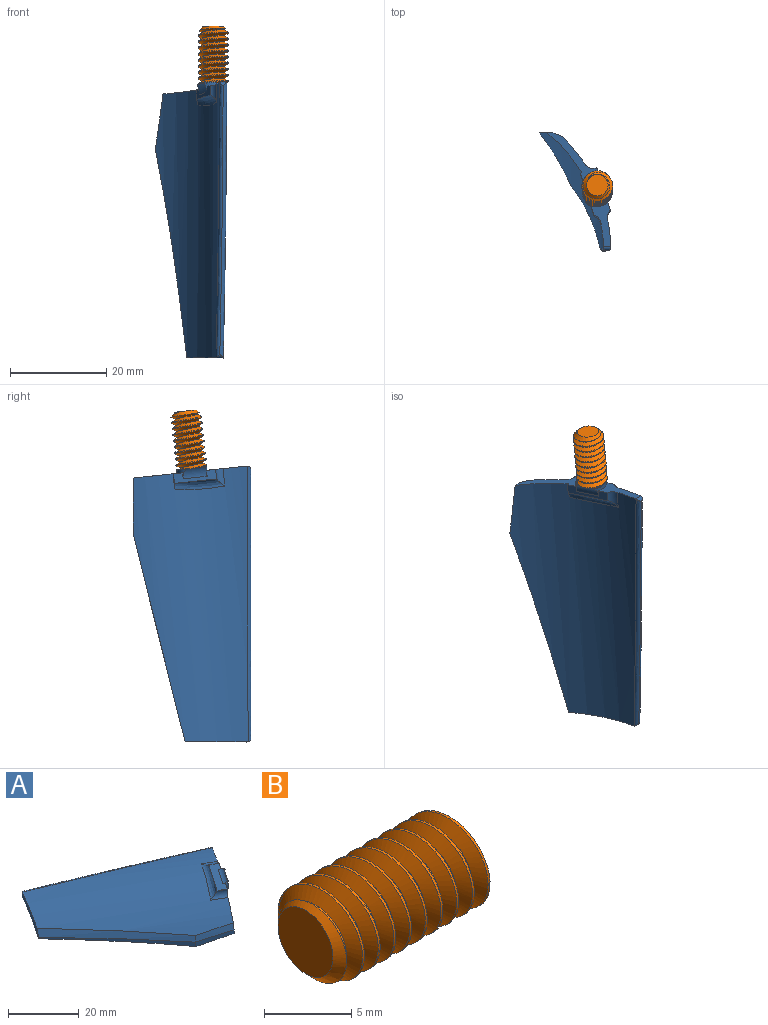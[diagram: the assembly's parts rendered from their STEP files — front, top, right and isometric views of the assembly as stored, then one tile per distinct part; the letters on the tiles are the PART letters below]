
ASSEMBLY  parts=2 mates=1
PART A: 35 faces, bbox 98.5x57.7x16.1 mm
  f0: cylinder r=31.75mm len=61.98mm, axis (0.87,-0.5,0), area 1229.6mm2, adj f8,f10,f11,f12,f13,f14,f15,f16
  f1: cylinder r=33.27mm len=61.61mm, axis (0.87,-0.5,0), area 1109.5mm2, adj f6,f7,f9,f11,f12,f15,f16,f19
  f2: cylinder r=3.17mm len=4.73mm, axis (-0.87,0.5,0), area 3.6mm2, adj f4,f5,f15,f17,f22,f26,f27
  f3: cylinder r=3.17mm len=4.72mm, axis (-0.87,0.5,0), area 3.6mm2, adj f4,f5,f16,f17,f22,f26,f28
  f4: plane 3.52x2.06mm, normal (-0.72,0.16,0.67), area 0.7mm2, adj f2,f3,f22,f27,f28,f29,f30,f31
  f5: plane 8.76x6.27mm, normal (0.15,0.27,-0.95), area 12mm2, adj f2,f3,f15,f16,f23,f24,f25,f26
  f6: bspline ~39.82x31.49mm, area 102.7mm2, adj f1,f7,f12,f13
  f7: bspline ~11.97x5.98mm, area 22.9mm2, adj f1,f6,f14,f16
  f8: cylinder r=0.76mm len=1.54mm, axis (0,0,1), area 1.2mm2, adj f0,f9,f10,f12
  f9: bspline ~98.35x44.27mm, area 73.1mm2, adj f1,f8,f10,f11,f12
  f10: bspline ~52.65x24.02mm, area 63mm2, adj f0,f8,f9,f11
  f11: cylinder r=0.76mm len=1.53mm, axis (0,0,-1), area 1.3mm2, adj f0,f1,f9,f10,f15
  f12: plane 11.9x7.69mm, normal (-0.91,0.41,0), area 21mm2, adj f0,f1,f6,f8,f9,f13
  f13: plane 35.31x27.6mm, normal (-0.62,-0.79,0), area 41.9mm2, adj f0,f6,f12,f14
  f14: plane 10.5x4.68mm, normal (-0.41,-0.91,0), area 15.8mm2, adj f0,f7,f13,f16
  f15: plane 8.28x4.78mm, normal (0.87,-0.5,0), area 17.8mm2, adj f0,f1,f2,f5,f11,f17,f21,f25
  f16: plane 10.96x8.97mm, normal (0.87,-0.5,0), area 22.1mm2, adj f0,f1,f3,f5,f7,f14,f17,f18
  f17: plane 9.2x7.07mm, normal (-0.15,-0.27,0.95), area 23.4mm2, adj f2,f3,f15,f16,f18,f20,f21,f22
  f18: plane 2.62x1.54mm, normal (-0.48,-0.82,-0.31), area 0.3mm2, adj f16,f17,f19,f20
  f19: cylinder r=2mm len=4.78mm, axis (0.87,-0.5,0), area 10.5mm2, adj f1,f16,f18,f20
  f20: bspline ~13.7x8.44mm, area 23.6mm2, adj f1,f17,f18,f19,f21
  f21: cylinder r=2mm len=5.09mm, axis (0.87,-0.5,0), area 7.9mm2, adj f1,f15,f17,f20
  f22: cylinder r=2mm len=5.2mm, axis (0.48,0.82,0.31), area 7.5mm2, adj f2,f3,f4,f17
  f23: plane 2.88x1.68mm, normal (-0.48,-0.82,-0.31), area 0.7mm2, adj f0,f5,f16,f24
  f24: bspline ~10.69x6.67mm, area 20.3mm2, adj f0,f5,f23,f25
  f25: cylinder r=2mm len=3.93mm, axis (-0.87,0.5,0), area 6.2mm2, adj f0,f5,f15,f24
  f26: cylinder r=3mm len=5.15mm, axis (0.48,0.82,0.31), area 10.3mm2, adj f2,f3,f5,f27,f28,f29,f30,f31
  f27: torus R=3.17mm, axis (0.87,-0.5,0), area 1.4mm2, adj f2,f4,f26,f30
  f28: torus R=3.17mm, axis (0.87,-0.5,0), area 1.4mm2, adj f3,f4,f26,f31
  f29: plane 5.79x5.24mm, normal (0.87,-0.5,0), area 26.2mm2, adj f4,f26,f30,f31
  f30: cylinder r=3.02mm len=5mm, axis (0.87,-0.5,0), area 0.9mm2, adj f4,f26,f27,f29
  f31: cylinder r=3.02mm len=5mm, axis (0.87,-0.5,0), area 0.9mm2, adj f4,f26,f28,f29
  f32: cylinder r=0.13mm len=0.57mm, axis (0.87,-0.5,0), area 0.4mm2, adj f33,f34
  f33: plane 0.25x0.22mm, normal (0.87,-0.5,0), area 0.1mm2, adj f32
  f34: plane 0.25x0.22mm, normal (-0.87,0.5,0), area 0.1mm2, adj f32
PART B: 8 faces, bbox 13.6x7x7 mm
  f0: cone r=3.17mm half-angle=45deg, axis (1,0,0), area 11.7mm2, adj f1,f3,f4,f5,f6
  f1: cone r=3.17mm half-angle=45deg, axis (1,0,0), area 0.6mm2, adj f0,f2,f4
  f2: cylinder r=3.17mm len=11.05mm, axis (1,0,0), area 27.6mm2, adj f1,f4,f6,f7
  f3: plane 4.45x4.45mm, normal (-1,0,0), area 15.5mm2, adj f0
  f4: bspline ~12.58x6.49mm, area 149.3mm2, adj f0,f1,f2,f5,f7
  f5: bspline ~12.38x4.7mm, area 21.9mm2, adj f0,f4,f6,f7
  f6: bspline ~13.06x6.49mm, area 149.2mm2, adj f0,f2,f5,f7
  f7: plane 6.05x6.01mm, normal (1,0,0), area 24.2mm2, adj f2,f4,f5,f6
PLACE A rot(axis=(-0.7,0.15,-0.7),163.1deg) t=(0.63,7.08,75.12)mm
PLACE B rot(axis=(-0.05,1,-0.05),90.2deg) t=(1.04,5.06,56.18)mm
MATE fastened B.f7 <-> A.f27  axis (0,-0.1,-0.99) through (0.63,5.16,56.87)mm
